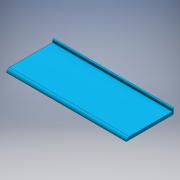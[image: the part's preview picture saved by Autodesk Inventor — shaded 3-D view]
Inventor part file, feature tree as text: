
AUTODESK INVENTOR PART (.ipt)
format: ipt  version: 2016 (Build 200138000, 138)  size: 138,240 bytes
history: native  units: mm
features: extrude x2, sketch x2, fillet x1
ambient origin geometry x8: Origin, YZ Plane, XZ Plane, XY Plane, X Axis, Y Axis, Z Axis, Center Point
bodies: Solid1 (feature_tree)
feature tree (5):
  extrude  "Extrusion1"  Depth=50.0mm TaperAngle=0.0deg
  fillet  "Fillet1"  Radius=50.0mm
  extrude  "Extrusion2"  Depth=20.0mm
  sketch  "Sketch1"  dims[d1=790.0mm d2=50.0mm d3=0.0mm d4=50.0mm]
  sketch  "Sketch2"  dims[d5=100.0mm d6=20.0mm d7=20.0mm d8=50.0mm d9=0.0mm]
